# Revit family: Deca_Torneira de mesa para cozinha_Deca Click_1191
name_source: partatom
category: Plumbing Fixtures
units: mm (PartAtom-declared; Revit-internal decimal feet)

## family parameters
Cut with Voids When Loaded = No
Host = Face
Part Type = Normal
Room Calculation Point = No
Round Connector Dimension = Use Radius
Shared = No

## types (5) — shared parameters
Acompanha o Produto = -
Aprovado por = quattroD
Atendimento ao Cliente = 0800-0117073
Categoria = METAIS PARA COZINHA
Composição Anel Vedação = -
Composição Assento = -
Composição Básica = Liga de Cobre (bronze e latão),Plásticos de Engenharia,Elastômeros
Composição Componente = -
Consumo = -
Cor Interna = -
Cor Secundária = -
Cores Componente = -
Criado por = quattroD
Código Pai = 1191
Description = Torneira de mesa para cozinha
Diâmetro Água Fria = 15 mm  [stored 0.0492126 ft]
Informações Complementares = -
Itens de Instalação = -
Linha = Deca Click
Manufacturer = Deca
Norma = NBR10281
Pressão máx. funcionamento = 40 MCA
Pressão mín. Aquec. Acúmulo = -
Pressão mín. Aquec. Passagem = -
Pressão mín. funcionamento = 2 MCA
Raio Água Fria = 8 mm  [stored 0.0262467 ft]
Saída de Esgoto = -
Segmento = Banheiro Luxo
Tipo de dispositivo economizador = Sim
Tipo de rosca de entrada = BSP NBR 8133
Tipo de rosca de saída = -
URL = www.deca.com.br
Vazão na Pressão máx. (L/min) = 6
Vazão na Pressão mín. (L/min) = 4
zero-valued in all types: CWFU, Default Elevation, HWFU, WFU

## per-type parameters (varying)
| type | Cor Principal | Model | Peso Líquido (Kg) | Tipo de mecanismo utilizado | Torneira |
| 1191.BL.MT_Black Matte | Black Matte | 1191.BL.MT | 2.55 | Mecanismo Click | Deca_Black Matte |
| 1191.C_Cromado | Cromado | 1191.C | 2.511 | Mecanismo MVC 1/4 de volta e Mecanismo Click | Deca_Cromado |
| 1191.CT.MT_Corten | Corten | 1191.CT.MT | 2.55 | Mecanismo Click | Deca_Corten |
| 1191.GL.RD_Red Gold | Red Gold | 1191.GL.RD | 2.511 | Mecanismo Click | Deca_Red Gold |
| 1191.INX_Inox | Inox | 1191.INX | 2.511 | Mecanismo Click | Deca_Inox |

note: source unit labels omitted for Vazão na Pressão máx. (L/min), Vazão na Pressão mín. (L/min) — the stored unit's dimension contradicts the parameter name (converter mislabeling)

note: [stored X ft] marks values corroborated as IEEE doubles in the binary element streams (Revit-internal decimal feet)

## geometry (parser evidence)
native form markers: Sweep x2
no freeform markers — native parametric forms only
